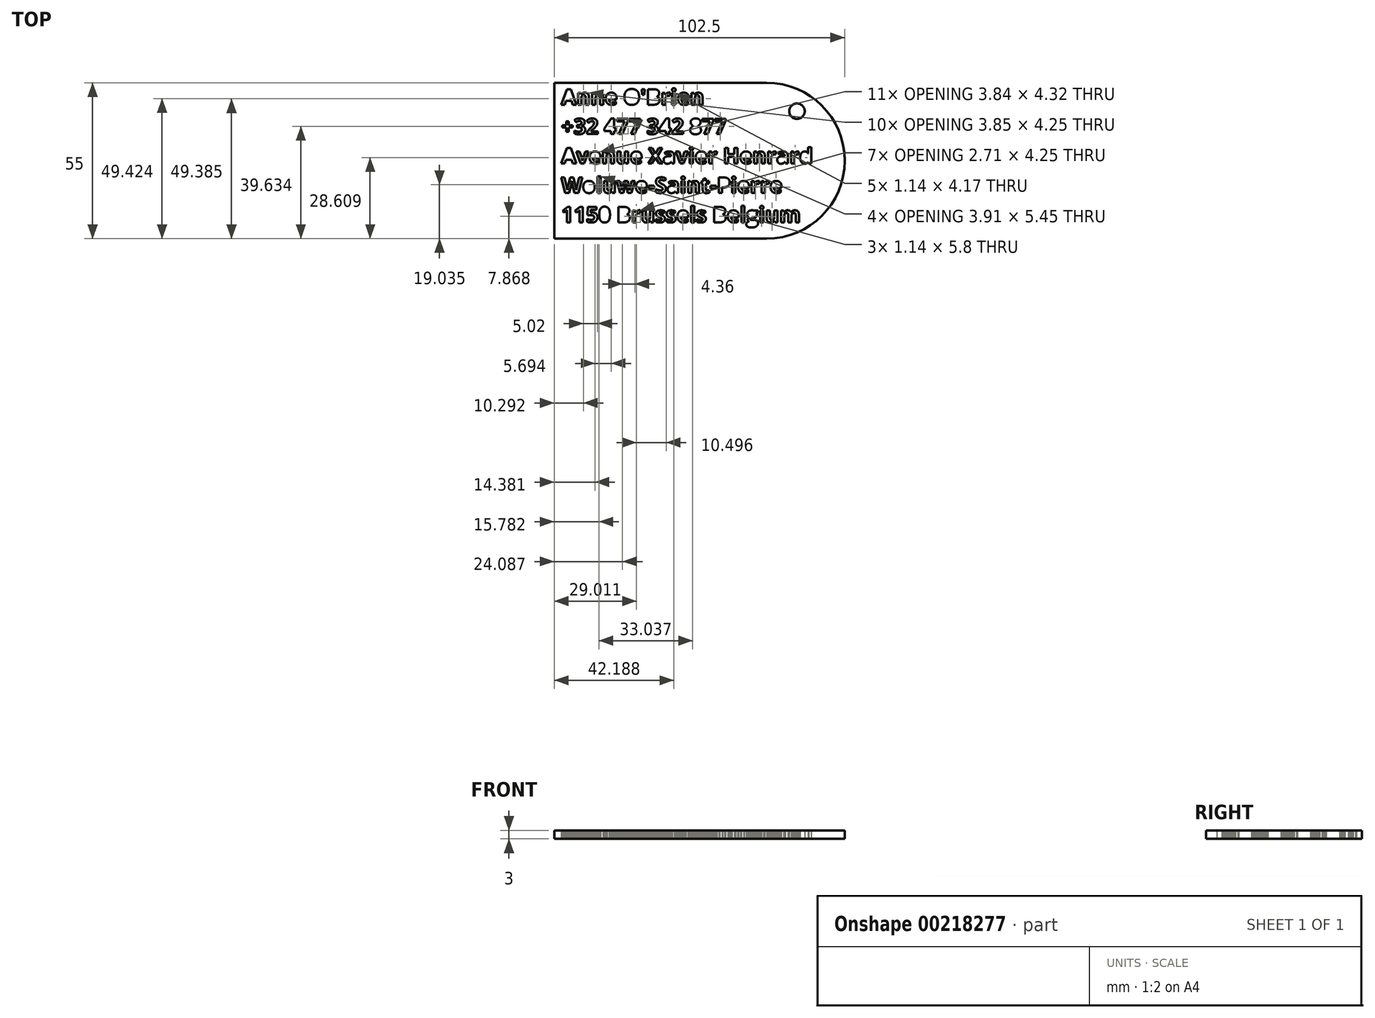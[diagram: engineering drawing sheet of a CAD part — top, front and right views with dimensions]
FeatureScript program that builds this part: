
annotation { "Feature Type Name" : "Feature", "Feature Type Description" : "" }
export const myFeature = defineFeature(function(context is Context, id is Id, definition is map)
    precondition{}
    {
        {
            var Q0;
            Q0=qCreatedBy(makeId("Top.planeOp"),FACE);
            var sketch = newSketch(context, id + "F0", { "sketchPlane" : qUnion([Q0])});
            skText(sketch, "E0", { "text": "Anne O\'Brien\n+32 477 342 877\nAvenue Xavier Henrard\nWoluwe-Saint-Pierre\n1150 Brussels Belgium", "fontName": "OpenSans-Bold.ttf"});
            skLineSegment(sketch, "E1.bottom", {"start": v(-17.56, 2.9) * mm, "end": v(57.44, 2.9) * mm});
            skLineSegment(sketch, "E1.top", {"start": v(-17.56, -52.1) * mm, "end": v(57.44, -52.1) * mm});
            skLineSegment(sketch, "E1.left", {"start": v(-17.56, 2.9) * mm, "end": v(-17.56, -52.1) * mm});
            skArc(sketch, "E2", {"start": v(57.44, -52.1) * mm, "mid": v(84.94, -24.6) * mm, "end": v(57.44, 2.9) * mm});
            skCircle(sketch, "E3", {"center": v(68.1, -7.1) * mm, "radius": 2.72 * mm});
            const initialGuessF0  = {"E0": [-0.01506, -0.0048, 1, 0, 0.0055]};
            skSetInitialGuess(sketch, initialGuessF0);
            skSolve(sketch);
        }
        {
            var Q0;
            Q0=makeQuery(id+"F0.imprint","IMPRINT",FACE,{"disambiguationData":[TD([[makeQuery(id+"F0.imprint","IMPRINT",EDGE,{"derivedFrom":sQuery(id+"F0.wireOp",EDGE,"E0.sketch_text.stroke-0")}),1.0]])]});
            extrude(context, id + "F1", {"entities" : qUnion([Q0]), "depth" : 3 * mm});
        }
    });
